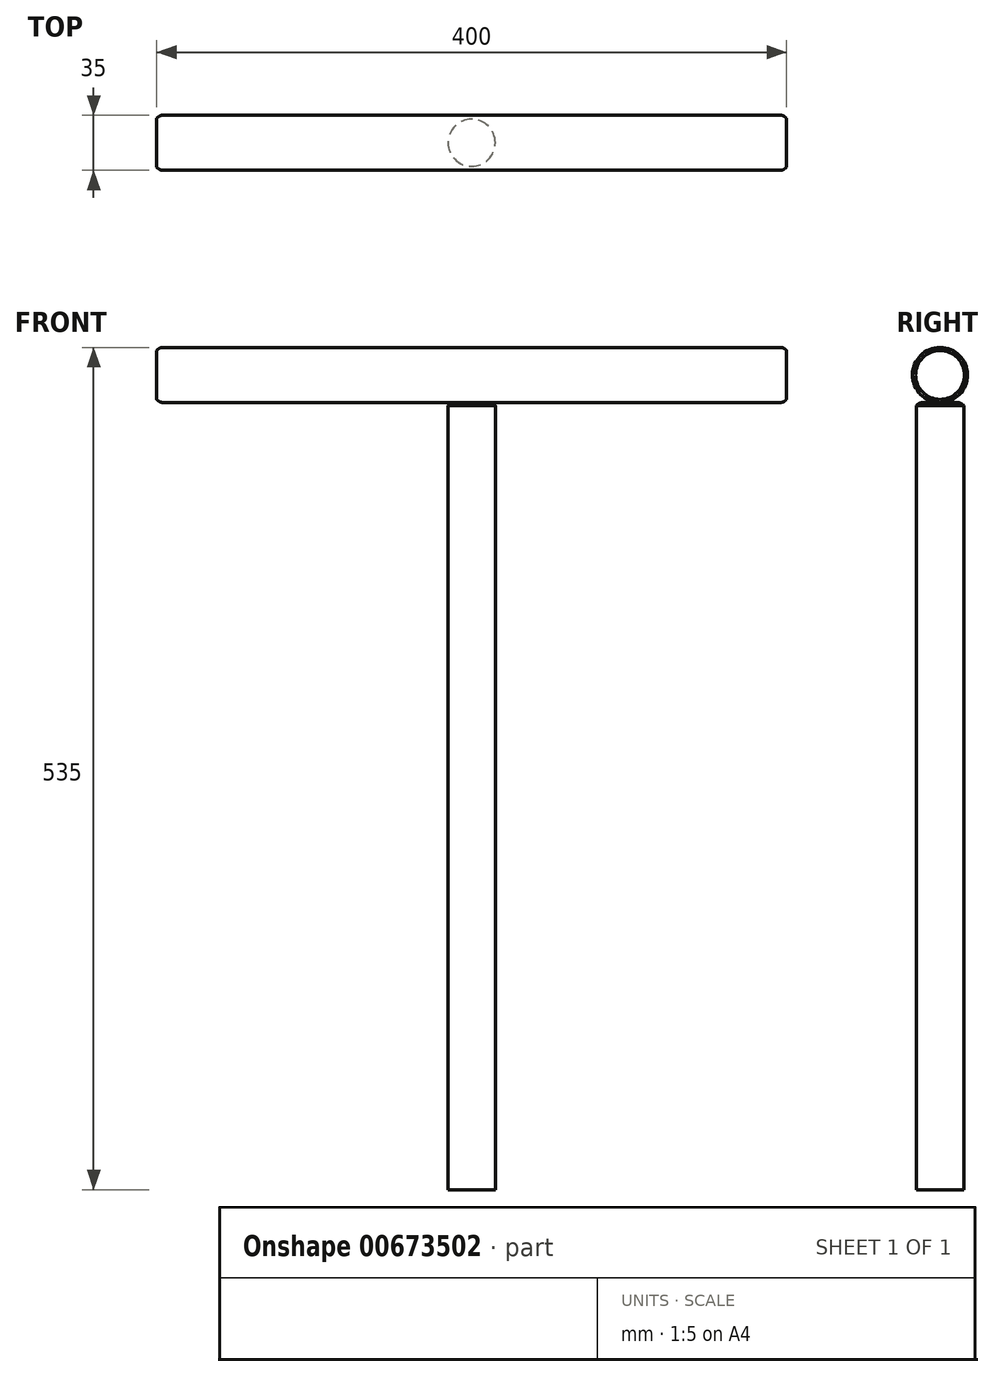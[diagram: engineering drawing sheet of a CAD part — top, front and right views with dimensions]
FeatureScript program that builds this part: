
annotation { "Feature Type Name" : "Feature", "Feature Type Description" : "" }
export const myFeature = defineFeature(function(context is Context, id is Id, definition is map)
    precondition{}
    {
        {
            var Q0;
            Q0=qCreatedBy(makeId("Top.planeOp"),FACE);
            var sketch = newSketch(context, id + "F0", { "sketchPlane" : qUnion([Q0])});
            skCircle(sketch, "E0", {"center": v(0, 0) * mm, "radius": 15 * mm});
            skSolve(sketch);
        }
        {
            var Q0;
            Q0=makeQuery(id+"F0.imprint","IMPRINT",FACE,{"disambiguationData":[TD([[makeQuery(id+"F0.imprint","IMPRINT",EDGE,{"derivedFrom":sQuery(id+"F0.wireOp",EDGE,"E0")}),1.0]])]});
            extrude(context, id + "F1", {"entities" : qUnion([Q0]), "oppositeDirection" : true, "depth" : 500 * mm, "offsetDistance" : 25 * mm});
        }
        {
            var Q0;
            Q0=qCreatedBy(makeId("Right.planeOp"),FACE);
            var sketch = newSketch(context, id + "F2", { "sketchPlane" : qUnion([Q0])});
            skCircle(sketch, "E1", {"center": v(0, 17.5) * mm, "radius": 17.5 * mm});
            skSolve(sketch);
        }
        {
            var Q0;
            Q0 = qSketchRegion(id + "F2", true);
            extrude(context, id + "F3", {"entities" : qUnion([Q0]), "operationType" : NewBodyOperationType.ADD, "endBound" : BoundingType.SYMMETRIC, "depth" : 400 * mm, "offsetDistance" : 25 * mm});
        }
        {
            var Q0;
            Q0=makeQuery(id+"F1.opExtrude","CAP_EDGE",EDGE,{"disambiguationData":[OSD([sQuery(id+"F0.wireOp",EDGE,"E0")])],"isStart":true});
            var Q1;
            Q1=makeQuery(id+"F3.opExtrude","SWEPT_FACE",FACE,{"disambiguationData":[OSD([sQuery(id+"F2.wireOp",EDGE,"E1")])]});
            chamfer(context, id + "F4", {"entities" : qUnion([Q0, Q1]), "width" : 2 * mm, "tangentPropagation" : true});
        }
        {
            var Q0;
            Q0=makeQuery(id+"F3.opExtrude","SWEPT_FACE",FACE,{"disambiguationData":[OSD([sQuery(id+"F2.wireOp",EDGE,"E1")])]});
            var Q1;
            {var subQ0=sQuery(id+"F0.wireOp",EDGE,"E0");Q1=makeQuery(id+"F4.opChamfer","BLEND_EDGE",EDGE,{"blendedFrom":[makeQuery(id+"F1.opExtrude","CAP_EDGE",EDGE,{"disambiguationData":[OSD([subQ0])],"isStart":true}),makeQuery(id+"F1.opExtrude","CAP_FACE",FACE,{"disambiguationData":[OSD([subQ0])],"isStart":true})],"blendedInto":[makeQuery(id+"F1.opExtrude","CAP_FACE",FACE,{"disambiguationData":[OSD([subQ0])],"isStart":true})]});}
            fillet(context, id + "F5", {"entities" : qUnion([Q0, Q1]), "radius" : 5 * mm, "tangentPropagation" : true, "allowEdgeOverflow" : false});
        }
    });
